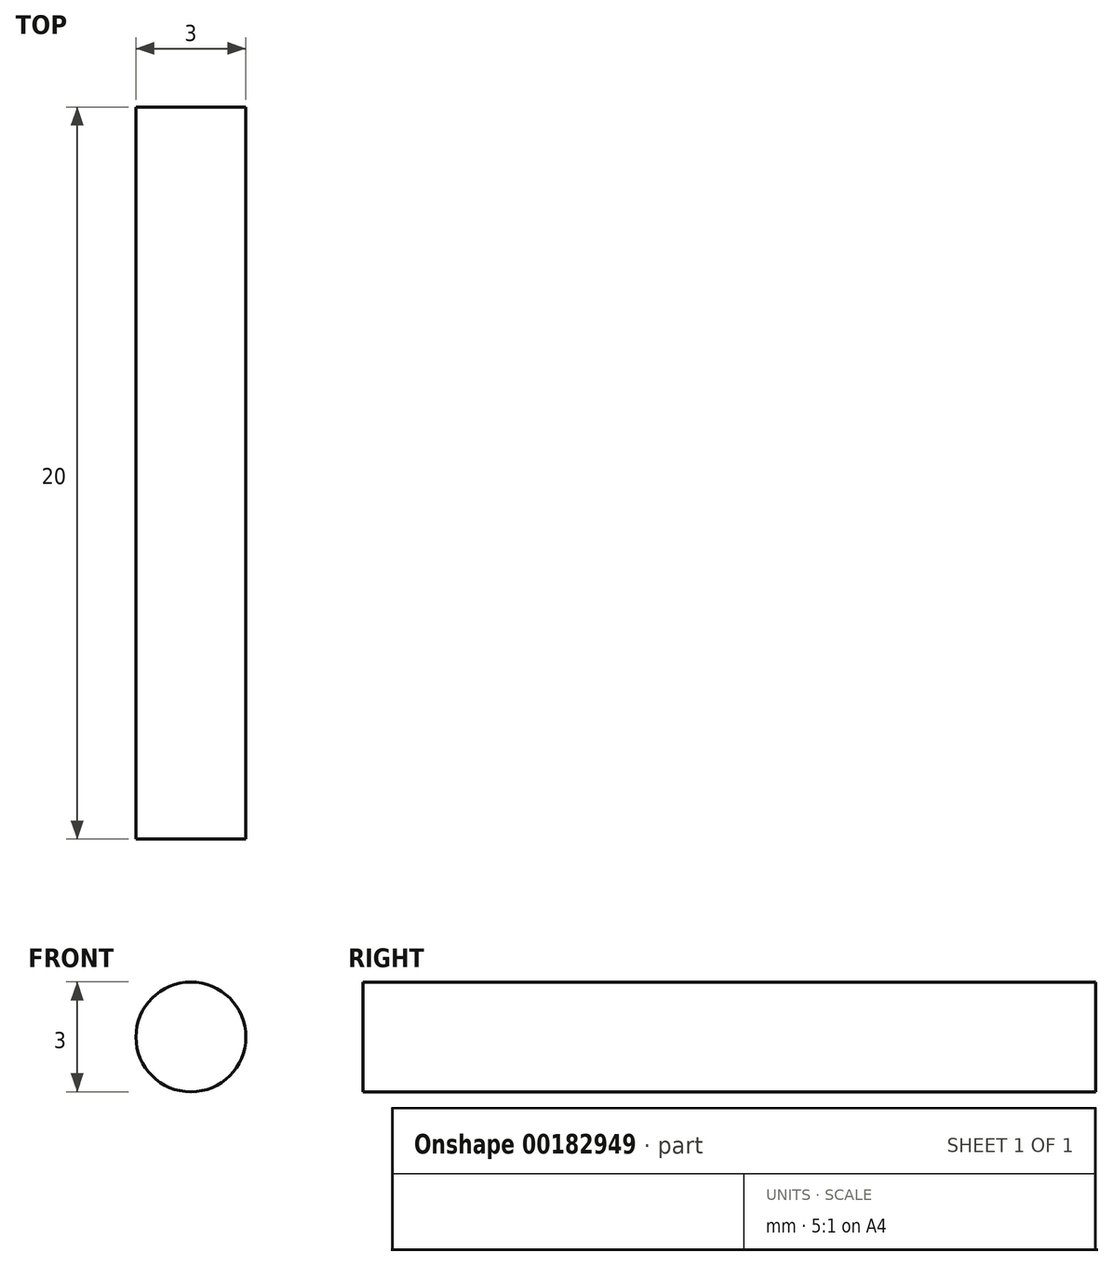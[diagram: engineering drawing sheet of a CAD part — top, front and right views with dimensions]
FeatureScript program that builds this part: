
annotation { "Feature Type Name" : "Feature", "Feature Type Description" : "" }
export const myFeature = defineFeature(function(context is Context, id is Id, definition is map)
    precondition{}
    {
        {
            var Q0;
            Q0=qCreatedBy(makeId("Front.planeOp"),FACE);
            var sketch = newSketch(context, id + "F0", { "sketchPlane" : qUnion([Q0])});
            skCircle(sketch, "E0", {"center": v(18.68, 12.5) * mm, "radius": 1.5 * mm});
            skSolve(sketch);
        }
        {
            var Q0;
            Q0=makeQuery(id+"F0.imprint","IMPRINT",FACE,{"disambiguationData":[TD([[makeQuery(id+"F0.imprint","IMPRINT",EDGE,{"derivedFrom":sQuery(id+"F0.wireOp",EDGE,"E0")}),1.0]])]});
            extrude(context, id + "F1", {"entities" : qUnion([Q0]), "depth" : 20 * mm});
        }
    });
